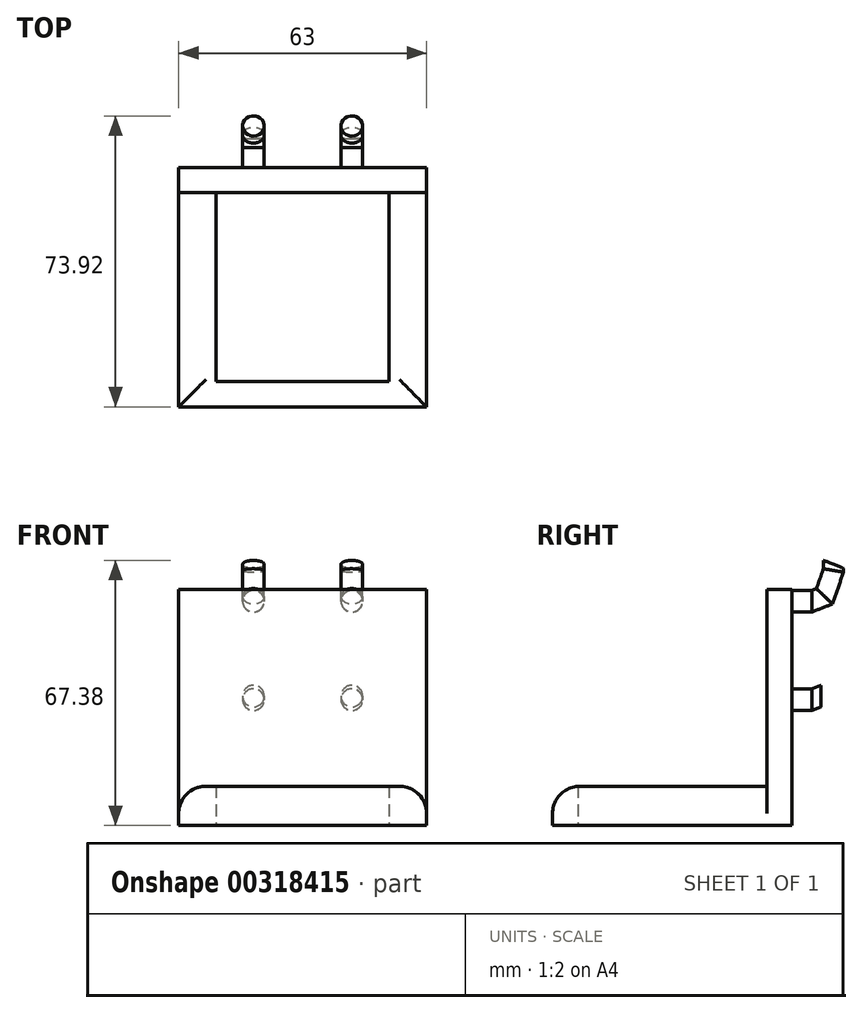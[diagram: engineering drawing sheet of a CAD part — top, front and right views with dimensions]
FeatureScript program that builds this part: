
annotation { "Feature Type Name" : "Feature", "Feature Type Description" : "" }
export const myFeature = defineFeature(function(context is Context, id is Id, definition is map)
    precondition{}
    {
        {
            var Q0;
            Q0=qCreatedBy(makeId("Top.planeOp"),FACE);
            var sketch = newSketch(context, id + "F0", { "sketchPlane" : qUnion([Q0])});
            skLineSegment(sketch, "E0.bottom", {"start": v(-31.5, 30.43) * mm, "end": v(31.5, 30.43) * mm});
            skLineSegment(sketch, "E0.top", {"start": v(-31.5, -30.43) * mm, "end": v(31.5, -30.43) * mm});
            skLineSegment(sketch, "E0.left", {"start": v(-31.5, 30.43) * mm, "end": v(-31.5, -30.43) * mm});
            skLineSegment(sketch, "E0.right", {"start": v(31.5, 30.43) * mm, "end": v(31.5, -30.43) * mm});
            skPoint(sketch, "E0.middle", {"position": v(0, 0) * mm});
            skLineSegment(sketch, "E1.bottom", {"start": v(22, 23.98) * mm, "end": v(-22, 23.98) * mm});
            skLineSegment(sketch, "E1.top", {"start": v(22, -23.98) * mm, "end": v(-22, -23.98) * mm});
            skLineSegment(sketch, "E1.left", {"start": v(22, 23.98) * mm, "end": v(22, -23.98) * mm});
            skLineSegment(sketch, "E1.right", {"start": v(-22, 23.98) * mm, "end": v(-22, -23.98) * mm});
            skSolve(sketch);
        }
        {
            var Q0;
            Q0 = qSketchRegion(id + "F0", true);
            extrude(context, id + "F1", {"entities" : qUnion([Q0]), "depth" : 10 * mm});
        }
        {
            var Q0;
            Q0=makeQuery(id+"F1.opExtrude","CAP_FACE",FACE,{"disambiguationData":[OSD([sQuery(id+"F0.wireOp",EDGE,"E0.bottom"),sQuery(id+"F0.wireOp",EDGE,"E0.top"),sQuery(id+"F0.wireOp",EDGE,"E0.left"),sQuery(id+"F0.wireOp",EDGE,"E0.right"),sQuery(id+"F0.wireOp",EDGE,"E1.bottom"),sQuery(id+"F0.wireOp",EDGE,"E1.top"),sQuery(id+"F0.wireOp",EDGE,"E1.left"),sQuery(id+"F0.wireOp",EDGE,"E1.right")])],"isStart":false});
            var sketch = newSketch(context, id + "F2", { "sketchPlane" : qUnion([Q0])});
            skLineSegment(sketch, "E2.bottom", {"start": v(-31.5, 30.43) * mm, "end": v(31.5, 30.43) * mm});
            skLineSegment(sketch, "E2.top", {"start": v(-31.5, 23.98) * mm, "end": v(31.5, 23.98) * mm});
            skLineSegment(sketch, "E2.left", {"start": v(-31.5, 30.43) * mm, "end": v(-31.5, 23.98) * mm});
            skLineSegment(sketch, "E2.right", {"start": v(31.5, 30.43) * mm, "end": v(31.5, 23.98) * mm});
            skSolve(sketch);
        }
        {
            var Q0;
            Q0 = qSketchRegion(id + "F2", true);
            extrude(context, id + "F3", {"entities" : qUnion([Q0]), "operationType" : NewBodyOperationType.ADD, "depth" : 50 * mm});
        }
        {
            var Q0;
            Q0=makeQuery(id+"F3.boolean.opBoolean","MERGE",FACE,{"derivedFrom":[makeQuery(id+"F1.opExtrude","SWEPT_FACE",FACE,{"disambiguationData":[OSD([sQuery(id+"F0.wireOp",EDGE,"E0.bottom")])]}),makeQuery(id+"F3.opExtrude","SWEPT_FACE",FACE,{"disambiguationData":[OSD([sQuery(id+"F2.wireOp",EDGE,"E2.bottom")])]})]});
            var sketch = newSketch(context, id + "F4", { "sketchPlane" : qUnion([Q0])});
            skCircle(sketch, "E3", {"center": v(-12.5, 57) * mm, "radius": 2.75 * mm});
            skCircle(sketch, "E4", {"center": v(-12.5, 32) * mm, "radius": 2.75 * mm});
            skCircle(sketch, "E5.MirrorC", {"center": v(12.5, 57) * mm, "radius": 2.75 * mm});
            skCircle(sketch, "E6.MirrorC", {"center": v(12.5, 32) * mm, "radius": 2.75 * mm});
            skSolve(sketch);
        }
        {
            var Q0;
            Q0 = qSketchRegion(id + "F4", true);
            extrude(context, id + "F5", {"entities" : qUnion([Q0]), "operationType" : NewBodyOperationType.ADD, "depth" : 5 * mm});
        }
        {
            var Q0;
            Q0=qCreatedBy(makeId("Right.planeOp"),FACE);
            var sketch = newSketch(context, id + "F6", { "sketchPlane" : qUnion([Q0])});
            skLineSegment(sketch, "E7", {"start": v(35.4, 56.99) * mm, "end": v(38.64, 58.26) * mm});
            skLineSegment(sketch, "E8", {"start": v(38.64, 58.26) * mm, "end": v(40.94, 64.83) * mm});
            skLineSegment(sketch, "E9", {"start": v(40.94, 64.83) * mm, "end": v(40.94, 66.37) * mm});
            skLineSegment(sketch, "E10", {"start": v(35.39, 32.1) * mm, "end": v(37.78, 33) * mm});
            skSolve(sketch);
        }
        {
            var Q0;
            Q0=makeQuery(id+"F5.opExtrude","CAP_FACE",FACE,{"disambiguationData":[OSD([sQuery(id+"F4.wireOp",EDGE,"E3")])],"isStart":false});
            var Q1;
            Q1=makeQuery(id+"F5.opExtrude","CAP_FACE",FACE,{"disambiguationData":[OSD([sQuery(id+"F4.wireOp",EDGE,"E5.MirrorC")])],"isStart":false});
            var Q2;
            Q2=sQuery(id+"F6.wireOp",EDGE,"E7");
            var Q3;
            Q3=sQuery(id+"F6.wireOp",EDGE,"E8");
            var Q4;
            Q4=sQuery(id+"F6.wireOp",EDGE,"E9");
            sweep(context, id + "F7", {"operationType" : NewBodyOperationType.ADD, "profiles" : qUnion([Q0, Q1]), "path" : qUnion([Q2, Q3, Q4])});
        }
        {
            var Q0;
            Q0=makeQuery(id+"F5.opExtrude","CAP_FACE",FACE,{"disambiguationData":[OSD([sQuery(id+"F4.wireOp",EDGE,"E4")])],"isStart":false});
            var Q1;
            Q1=makeQuery(id+"F5.opExtrude","CAP_FACE",FACE,{"disambiguationData":[OSD([sQuery(id+"F4.wireOp",EDGE,"E6.MirrorC")])],"isStart":false});
            var Q2;
            Q2 = qSketchRegion(id + "F6", true);
            var Q3;
            Q3=sQuery(id+"F6.wireOp",EDGE,"E10");
            sweep(context, id + "F8", {"operationType" : NewBodyOperationType.ADD, "profiles" : qUnion([Q0, Q1, Q2]), "path" : qUnion([Q3])});
        }
        {
            var Q0;
            Q0=makeQuery(id+"F1.opExtrude","CAP_EDGE",EDGE,{"disambiguationData":[OSD([sQuery(id+"F0.wireOp",EDGE,"E0.left")])],"isStart":false});
            var Q1;
            Q1=makeQuery(id+"F1.opExtrude","CAP_EDGE",EDGE,{"disambiguationData":[OSD([sQuery(id+"F0.wireOp",EDGE,"E0.right")])],"isStart":false});
            var Q2;
            Q2=makeQuery(id+"F1.opExtrude","CAP_EDGE",EDGE,{"disambiguationData":[OSD([sQuery(id+"F0.wireOp",EDGE,"E0.top")])],"isStart":false});
            fillet(context, id + "F9", {"entities" : qUnion([Q0, Q1, Q2]), "radius" : 6.9 * mm, "tangentPropagation" : true, "allowEdgeOverflow" : false});
        }
    });
